annotation { "Feature Type Name" : "Feature", "Feature Type Description" : "" }
export const myFeature = defineFeature(function(context is Context, id is Id, definition is map)
    precondition{}
    {
        {
            var Q0;
            Q0=qCreatedBy(makeId("Front.planeOp"),FACE);
            var sketch = newSketch(context, id + "F0", { "sketchPlane" : qUnion([Q0])});
            skLineSegment(sketch, "E0", {"start": v(0, 0) * mm, "end": v(-4572, 0) * mm});
            skLineSegment(sketch, "E1", {"start": v(0, 0) * mm, "end": v(4572, 0) * mm});
            skLineSegment(sketch, "E2", {"start": v(0, 0) * mm, "end": v(0, 2286) * mm});
            skLineSegment(sketch, "E3", {"start": v(0, 2286) * mm, "end": v(4572, 0) * mm});
            skLineSegment(sketch, "E4", {"start": v(0, 2286) * mm, "end": v(-4572, 0) * mm});
            skLineSegment(sketch, "E5", {"start": v(-4572, 0) * mm, "end": v(-4572, -3352.8) * mm});
            skLineSegment(sketch, "E6", {"start": v(4572, 0) * mm, "end": v(4572, -3352.8) * mm});
            skLineSegment(sketch, "E7", {"start": v(0, 2286) * mm, "end": v(0, 2743.2) * mm});
            skLineSegment(sketch, "E8", {"start": v(0, 2743.2) * mm, "end": v(-5486.4, 0) * mm});
            skLineSegment(sketch, "E9", {"start": v(-5486.4, 0) * mm, "end": v(-4572, 0) * mm});
            skLineSegment(sketch, "E10", {"start": v(4572, 0) * mm, "end": v(5486.4, 0) * mm});
            skLineSegment(sketch, "E11", {"start": v(0, 2743.2) * mm, "end": v(5486.4, 0) * mm});
            skLineSegment(sketch, "E12", {"start": v(-4572, -3352.8) * mm, "end": v(4572, -3352.8) * mm});
            skLineSegment(sketch, "E13", {"start": v(-4572, -3352.8) * mm, "end": v(-4572, -3962.4) * mm});
            skLineSegment(sketch, "E14", {"start": v(-4572, -3962.4) * mm, "end": v(4572, -3962.4) * mm});
            skLineSegment(sketch, "E15", {"start": v(4572, -3962.4) * mm, "end": v(4572, -3352.8) * mm});
            skLineSegment(sketch, "E16", {"start": v(4572, -3352.8) * mm, "end": v(9144, -3352.8) * mm});
            skLineSegment(sketch, "E17", {"start": v(4572, -3962.4) * mm, "end": v(9144, -3962.4) * mm});
            skLineSegment(sketch, "E18", {"start": v(9144, -3962.4) * mm, "end": v(9144, -3352.8) * mm});
            skLineSegment(sketch, "E19", {"start": v(4572, 0) * mm, "end": v(9144, -603.23) * mm});
            skLineSegment(sketch, "E20", {"start": v(4572, 0) * mm, "end": v(4572, -609.6) * mm});
            skLineSegment(sketch, "E21", {"start": v(4572, -609.6) * mm, "end": v(9144, -1212.83) * mm});
            skLineSegment(sketch, "E22", {"start": v(9144, -603.23) * mm, "end": v(9144, -3352.8) * mm});
            skLineSegment(sketch, "E23.bottom", {"start": v(223.55, -1010.7) * mm, "end": v(2966.75, -1010.7) * mm});
            skLineSegment(sketch, "E23.top", {"start": v(223.55, -2382.3) * mm, "end": v(2966.75, -2382.3) * mm});
            skLineSegment(sketch, "E23.left", {"start": v(223.55, -1010.7) * mm, "end": v(223.55, -2382.3) * mm});
            skLineSegment(sketch, "E23.right", {"start": v(2966.75, -1010.7) * mm, "end": v(2966.75, -2382.3) * mm});
            skLineSegment(sketch, "E24.0", {"start": v(71.15, -858.3) * mm, "end": v(3119.15, -858.3) * mm});
            skLineSegment(sketch, "E24.1", {"start": v(71.15, -858.3) * mm, "end": v(71.15, -2534.7) * mm});
            skLineSegment(sketch, "E24.2", {"start": v(71.15, -2534.7) * mm, "end": v(3119.15, -2534.7) * mm});
            skLineSegment(sketch, "E24.3", {"start": v(3119.15, -858.3) * mm, "end": v(3119.15, -2534.7) * mm});
            skLineSegment(sketch, "E25", {"start": v(-1104.35, 2191.03) * mm, "end": v(-1104.35, 4324.63) * mm});
            skLineSegment(sketch, "E26", {"start": v(-1104.35, 4324.63) * mm, "end": v(0, 4324.63) * mm});
            skLineSegment(sketch, "E27", {"start": v(0, 2743.2) * mm, "end": v(0, 4324.63) * mm});
            skLineSegment(sketch, "E28.bottom", {"start": v(6709.8, -1486.73) * mm, "end": v(7929, -1486.73) * mm});
            skLineSegment(sketch, "E28.top", {"start": v(6709.8, -2705.93) * mm, "end": v(7929, -2705.93) * mm});
            skLineSegment(sketch, "E28.left", {"start": v(6709.8, -1486.73) * mm, "end": v(6709.8, -2705.93) * mm});
            skLineSegment(sketch, "E28.right", {"start": v(7929, -1486.73) * mm, "end": v(7929, -2705.93) * mm});
            skLineSegment(sketch, "E29.0", {"start": v(6557.4, -1334.33) * mm, "end": v(8081.4, -1334.33) * mm});
            skLineSegment(sketch, "E29.1", {"start": v(6557.4, -1334.33) * mm, "end": v(6557.4, -2858.33) * mm});
            skLineSegment(sketch, "E29.2", {"start": v(6557.4, -2858.33) * mm, "end": v(8081.4, -2858.33) * mm});
            skLineSegment(sketch, "E29.3", {"start": v(8081.4, -1334.33) * mm, "end": v(8081.4, -2858.33) * mm});
            skLineSegment(sketch, "E30.bottom", {"start": v(-3438.86, -3352.8) * mm, "end": v(-2524.46, -3352.8) * mm});
            skLineSegment(sketch, "E30.top", {"start": v(-3438.86, -1219.2) * mm, "end": v(-2524.46, -1219.2) * mm});
            skLineSegment(sketch, "E30.left", {"start": v(-3438.86, -3352.8) * mm, "end": v(-3438.86, -1219.2) * mm});
            skLineSegment(sketch, "E30.right", {"start": v(-2524.46, -3352.8) * mm, "end": v(-2524.46, -1219.2) * mm});
            skLineSegment(sketch, "E31.0", {"start": v(-2219.66, -3352.8) * mm, "end": v(-2219.66, -914.4) * mm});
            skLineSegment(sketch, "E31.1", {"start": v(-3743.66, -914.4) * mm, "end": v(-2219.66, -914.4) * mm});
            skLineSegment(sketch, "E31.2", {"start": v(-3743.66, -3352.8) * mm, "end": v(-3743.66, -914.4) * mm});
            skText(sketch, "E32", { "text": "Greta Branz", "fontName": "OpenSans-Italic.ttf"});
            const initialGuessF0  = {"E32": [1.34454, 4.86904, 1, 0, 1.43638]};
            skSetInitialGuess(sketch, initialGuessF0);
            skSolve(sketch);
        }
        {
            var Q0;
            Q0=makeQuery(id+"F0.imprint","IMPRINT",FACE,{"disambiguationData":[TD([[makeQuery(id+"F0.imprint","IMPRINT",EDGE,{"derivedFrom":sQuery(id+"F0.wireOp",EDGE,"E4")}),-1.0]])]});
            var Q1;
            Q1=makeQuery(id+"F0.imprint","IMPRINT",FACE,{"disambiguationData":[TD([[makeQuery(id+"F0.imprint","IMPRINT",EDGE,{"derivedFrom":sQuery(id+"F0.wireOp",EDGE,"E3")}),1.0]])]});
            var Q2;
            {var subQ0=sQuery(id+"F0.wireOp",EDGE,"E19");Q2=makeQuery(id+"F0.imprint","IMPRINT",FACE,{"disambiguationData":[TD([[makeQuery(id+"F0.imprint","IMPRINT",EDGE,{"derivedFrom":subQ0}),-1.0]])]});}
            extrude(context, id + "F1", {"entities" : qUnion([Q0, Q1, Q2]), "depth" : 914.4 * mm, "offsetDistance" : 30.48 * mm, "hasSecondDirection" : true, "secondDirectionOppositeDirection" : true, "secondDirectionDepth" : 12192 * mm});
        }
        {
            var Q0;
            Q0=makeQuery(id+"F0.imprint","IMPRINT",FACE,{"disambiguationData":[TD([[makeQuery(id+"F0.imprint","IMPRINT",EDGE,{"derivedFrom":sQuery(id+"F0.wireOp",EDGE,"E0")}),-1.0]])]});
            var Q1;
            Q1=makeQuery(id+"F0.imprint","IMPRINT",FACE,{"disambiguationData":[TD([[makeQuery(id+"F0.imprint","IMPRINT",EDGE,{"derivedFrom":sQuery(id+"F0.wireOp",EDGE,"E1")}),1.0]])]});
            extrude(context, id + "F2", {"entities" : qUnion([Q0, Q1]), "operationType" : NewBodyOperationType.ADD, "depth" : 30.48 * mm, "offsetDistance" : 30.48 * mm, "hasSecondDirection" : true, "secondDirectionOppositeDirection" : true, "secondDirectionDepth" : 12192 * mm});
        }
        {
            var Q0;
            {var subQ2=sQuery(id+"F0.wireOp",EDGE,"E25");Q0=makeQuery(id+"F0.imprint","IMPRINT",FACE,{"disambiguationData":[TD([[makeQuery(id+"F0.imprint","IMPRINT",EDGE,{"derivedFrom":subQ2}),-1.0]])]});}
            extrude(context, id + "F3", {"entities" : qUnion([Q0]), "operationType" : NewBodyOperationType.ADD, "depth" : 152.4 * mm, "offsetDistance" : 30.48 * mm, "hasSecondDirection" : true, "secondDirectionOppositeDirection" : true, "secondDirectionDepth" : 731.52 * mm});
        }
        {
            var Q0;
            {var subQ5=sQuery(id+"F0.wireOp",EDGE,"E13");Q0=makeQuery(id+"F0.imprint","IMPRINT",FACE,{"disambiguationData":[TD([[makeQuery(id+"F0.imprint","IMPRINT",EDGE,{"derivedFrom":subQ5}),1.0]])]});}
            var Q1;
            Q1=makeQuery(id+"F0.imprint","IMPRINT",FACE,{"disambiguationData":[TD([[makeQuery(id+"F0.imprint","IMPRINT",EDGE,{"derivedFrom":sQuery(id+"F0.wireOp",EDGE,"E15")}),-1.0]])]});
            extrude(context, id + "F4", {"entities" : qUnion([Q0, Q1]), "depth" : 3048 * mm, "offsetDistance" : 30.48 * mm, "hasSecondDirection" : true, "secondDirectionOppositeDirection" : true, "secondDirectionDepth" : 12192 * mm});
        }
        {
            var Q0;
            Q0=makeQuery(id+"F0.imprint","IMPRINT",FACE,{"disambiguationData":[TD([[makeQuery(id+"F0.imprint","IMPRINT",EDGE,{"derivedFrom":sQuery(id+"F0.wireOp",EDGE,"E0")}),1.0]])]});
            var Q1;
            Q1=makeQuery(id+"F0.imprint","IMPRINT",FACE,{"disambiguationData":[TD([[makeQuery(id+"F0.imprint","IMPRINT",EDGE,{"derivedFrom":sQuery(id+"F0.wireOp",EDGE,"E6")}),1.0]])]});
            var Q2;
            Q2=makeQuery(id+"F0.imprint","IMPRINT",FACE,{"disambiguationData":[TD([[makeQuery(id+"F0.imprint","IMPRINT",EDGE,{"derivedFrom":sQuery(id+"F0.wireOp",EDGE,"E28.bottom")}),-1.0]])]});
            var Q3;
            Q3=makeQuery(id+"F0.imprint","IMPRINT",FACE,{"disambiguationData":[TD([[makeQuery(id+"F0.imprint","IMPRINT",EDGE,{"derivedFrom":sQuery(id+"F0.wireOp",EDGE,"E23.bottom")}),-1.0]])]});
            var Q4;
            Q4=makeQuery(id+"F0.imprint","IMPRINT",FACE,{"disambiguationData":[TD([[makeQuery(id+"F0.imprint","IMPRINT",EDGE,{"derivedFrom":sQuery(id+"F0.wireOp",EDGE,"E30.bottom")}),1.0]])]});
            var Q5;
            Q5=makeQuery(id+"F0.imprint","IMPRINT",FACE,{"disambiguationData":[TD([[makeQuery(id+"F0.imprint","IMPRINT",EDGE,{"derivedFrom":sQuery(id+"F0.wireOp",EDGE,"E30.top")}),1.0]])]});
            var Q6;
            Q6=makeQuery(id+"F0.imprint","IMPRINT",FACE,{"disambiguationData":[TD([[makeQuery(id+"F0.imprint","IMPRINT",EDGE,{"derivedFrom":sQuery(id+"F0.wireOp",EDGE,"E23.bottom")}),1.0]])]});
            var Q7;
            Q7=makeQuery(id+"F0.imprint","IMPRINT",FACE,{"disambiguationData":[TD([[makeQuery(id+"F0.imprint","IMPRINT",EDGE,{"derivedFrom":sQuery(id+"F0.wireOp",EDGE,"E28.bottom")}),1.0]])]});
            extrude(context, id + "F5", {"entities" : qUnion([Q0, Q1, Q2, Q3, Q4, Q5, Q6, Q7]), "depth" : 30.48 * mm, "offsetDistance" : 30.48 * mm, "hasSecondDirection" : true, "secondDirectionOppositeDirection" : true, "secondDirectionDepth" : 12192 * mm});
        }
        {
            var Q0;
            Q0=makeQuery(id+"F0.imprint","IMPRINT",FACE,{"disambiguationData":[TD([[makeQuery(id+"F0.imprint","IMPRINT",EDGE,{"derivedFrom":sQuery(id+"F0.wireOp",EDGE,"E30.top")}),1.0]])]});
            extrude(context, id + "F6", {"entities" : qUnion([Q0]), "depth" : 30.48 * mm, "offsetDistance" : 30.48 * mm, "hasSecondDirection" : true, "secondDirectionOppositeDirection" : true, "secondDirectionDepth" : 152.4 * mm});
        }
        {
            var Q0;
            Q0=makeQuery(id+"F0.imprint","IMPRINT",FACE,{"disambiguationData":[TD([[makeQuery(id+"F0.imprint","IMPRINT",EDGE,{"derivedFrom":sQuery(id+"F0.wireOp",EDGE,"E23.bottom")}),1.0]])]});
            var Q1;
            Q1=makeQuery(id+"F0.imprint","IMPRINT",FACE,{"disambiguationData":[TD([[makeQuery(id+"F0.imprint","IMPRINT",EDGE,{"derivedFrom":sQuery(id+"F0.wireOp",EDGE,"E28.bottom")}),1.0]])]});
            extrude(context, id + "F7", {"entities" : qUnion([Q0, Q1]), "operationType" : NewBodyOperationType.ADD, "depth" : 152.4 * mm, "offsetDistance" : 30.48 * mm});
        }
        {
            var Q0;
            Q0=makeQuery(id+"F5.opExtrude","SWEPT_FACE",FACE,{"disambiguationData":[OSD([sQuery(id+"F0.wireOp",EDGE,"E5")])]});
            var sketch = newSketch(context, id + "F8", { "sketchPlane" : qUnion([Q0])});
            skLineSegment(sketch, "E33.bottom", {"start": v(-9906, -762) * mm, "end": v(-8077.2, -762) * mm});
            skLineSegment(sketch, "E33.top", {"start": v(-9906, -2590.8) * mm, "end": v(-8077.2, -2590.8) * mm});
            skLineSegment(sketch, "E33.left", {"start": v(-9906, -762) * mm, "end": v(-9906, -2590.8) * mm});
            skLineSegment(sketch, "E33.right", {"start": v(-8077.2, -762) * mm, "end": v(-8077.2, -2590.8) * mm});
            skLineSegment(sketch, "E34.0", {"start": v(-10058.4, -609.6) * mm, "end": v(-7924.8, -609.6) * mm});
            skLineSegment(sketch, "E34.1", {"start": v(-10058.4, -609.6) * mm, "end": v(-10058.4, -2743.2) * mm});
            skLineSegment(sketch, "E34.2", {"start": v(-10058.4, -2743.2) * mm, "end": v(-7924.8, -2743.2) * mm});
            skLineSegment(sketch, "E34.3", {"start": v(-7924.8, -609.6) * mm, "end": v(-7924.8, -2743.2) * mm});
            skLineSegment(sketch, "E35.bottom", {"start": v(-5303.52, -1066.8) * mm, "end": v(-2255.52, -1066.8) * mm});
            skLineSegment(sketch, "E35.top", {"start": v(-5303.52, -2590.8) * mm, "end": v(-2255.52, -2590.8) * mm});
            skLineSegment(sketch, "E35.left", {"start": v(-5303.52, -1066.8) * mm, "end": v(-5303.52, -2590.8) * mm});
            skLineSegment(sketch, "E35.right", {"start": v(-2255.52, -1066.8) * mm, "end": v(-2255.52, -2590.8) * mm});
            skLineSegment(sketch, "E36.0", {"start": v(-5455.92, -914.4) * mm, "end": v(-2103.12, -914.4) * mm});
            skLineSegment(sketch, "E36.1", {"start": v(-5455.92, -914.4) * mm, "end": v(-5455.92, -2743.2) * mm});
            skLineSegment(sketch, "E36.2", {"start": v(-5455.92, -2743.2) * mm, "end": v(-2103.12, -2743.2) * mm});
            skLineSegment(sketch, "E36.3", {"start": v(-2103.12, -914.4) * mm, "end": v(-2103.12, -2743.2) * mm});
            skSolve(sketch);
        }
        {
            var Q0;
            Q0=makeQuery(id+"F8.imprint","IMPRINT",FACE,{"disambiguationData":[TD([[makeQuery(id+"F8.imprint","IMPRINT",EDGE,{"derivedFrom":sQuery(id+"F8.wireOp",EDGE,"E35.bottom")}),1.0]])]});
            var Q1;
            Q1=makeQuery(id+"F8.imprint","IMPRINT",FACE,{"disambiguationData":[TD([[makeQuery(id+"F8.imprint","IMPRINT",EDGE,{"derivedFrom":sQuery(id+"F8.wireOp",EDGE,"E33.bottom")}),1.0]])]});
            var Q2;
            Q2=makeQuery(id+"F1.opExtrude","SWEPT_FACE",FACE,{"disambiguationData":[OSD([sQuery(id+"F0.wireOp",EDGE,"E8")])]});
            extrude(context, id + "F9", {"entities" : qUnion([Q0, Q1, Q2]), "depth" : 152.4 * mm, "offsetDistance" : 30.48 * mm});
        }
        {
            var Q0;
            Q0=makeQuery(id+"F4.opExtrude","SWEPT_FACE",FACE,{"disambiguationData":[OSD([sQuery(id+"F0.wireOp",EDGE,"E12"),sQuery(id+"F0.wireOp",EDGE,"E16"),sQuery(id+"F0.wireOp",EDGE,"E30.bottom")])]});
            var sketch = newSketch(context, id + "F10", { "sketchPlane" : qUnion([Q0])});
            skText(sketch, "E37", { "text": "Greta Branz", "fontName": "OpenSans-Italic.ttf"});
            const initialGuessF10  = {"E37": [-3.29455, -1.45773, 1, 0, 1.45773]};
            skSetInitialGuess(sketch, initialGuessF10);
            skSolve(sketch);
        }
        {
            var Q0;
            Q0 = qSketchRegion(id + "F10", true);
            extrude(context, id + "F11", {"entities" : qUnion([Q0]), "depth" : 304.8 * mm, "offsetDistance" : 30.48 * mm});
        }
    });